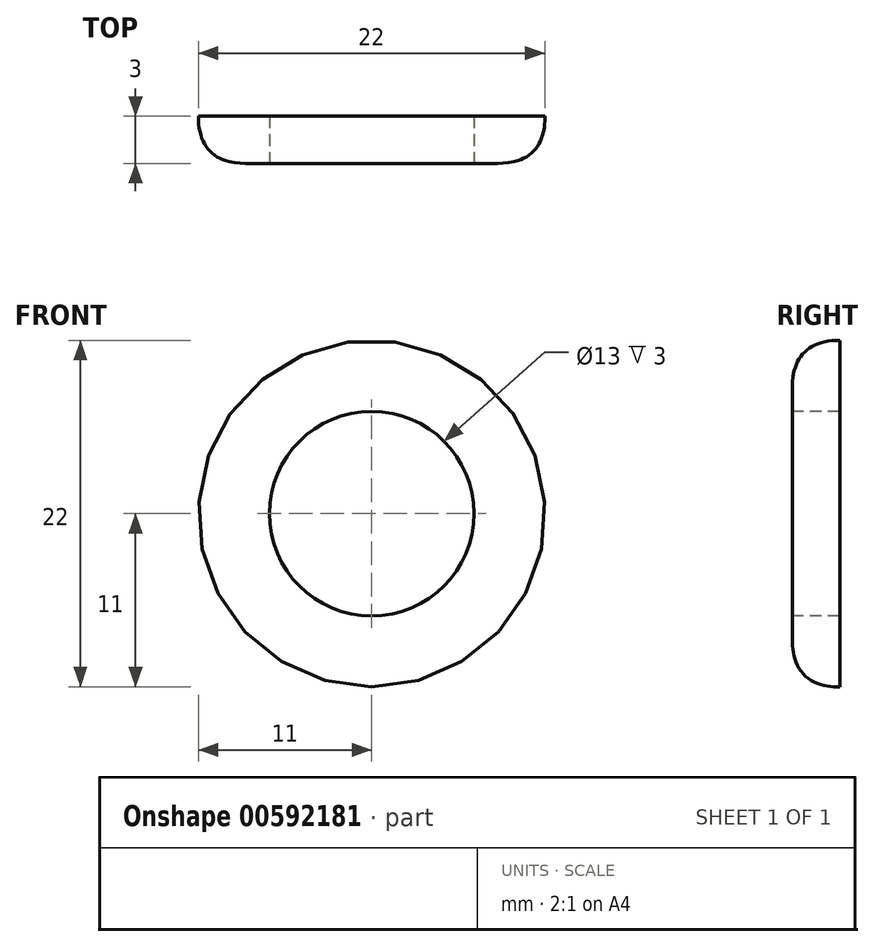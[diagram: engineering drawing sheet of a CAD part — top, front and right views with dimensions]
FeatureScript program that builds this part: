
annotation { "Feature Type Name" : "Feature", "Feature Type Description" : "" }
export const myFeature = defineFeature(function(context is Context, id is Id, definition is map)
    precondition{}
    {
        {
            var Q0;
            Q0=qCreatedBy(makeId("Front.planeOp"),FACE);
            var sketch = newSketch(context, id + "F0", { "sketchPlane" : qUnion([Q0])});
            skCircle(sketch, "E0", {"center": v(0, 0) * mm, "radius": 11 * mm});
            skSolve(sketch);
        }
        {
            var Q0;
            Q0 = qSketchRegion(id + "F0", true);
            extrude(context, id + "F1", {"entities" : qUnion([Q0]), "depth" : 3 * mm, "offsetDistance" : 25 * mm});
        }
        {
            var Q0;
            Q0=makeQuery(id+"F1.opExtrude","CAP_EDGE",EDGE,{"disambiguationData":[OSD([sQuery(id+"F0.wireOp",EDGE,"E0")])],"isStart":false});
            fillet(context, id + "F2", {"entities" : qUnion([Q0]), "tangentPropagation" : true, "crossSection" : FilletCrossSection.CURVATURE, "radius" : 3 * mm, "magnitude" : 0.5, "defaultsChanged" : false, "vertexSettings" : []});
        }
        {
            var Q0;
            Q0=makeQuery(id+"F1.opExtrude","CAP_FACE",FACE,{"disambiguationData":[OSD([sQuery(id+"F0.wireOp",EDGE,"E0")])],"isStart":false});
            var sketch = newSketch(context, id + "F3", { "sketchPlane" : qUnion([Q0])});
            skCircle(sketch, "E1", {"center": v(0, 0) * mm, "radius": 8 * mm});
            skSolve(sketch);
        }
        {
            var Q0;
            Q0=sQuery(id+"F3.wireOp",VERTEX,"E1.center");
            var Q1;
            Q1=makeQuery(id+"F1.opExtrude","SWEPT_BODY",BODY,{"disambiguationData":[OSD([sQuery(id+"F0.wireOp",EDGE,"E0")])]});
            hole(context, id + "F4", {"style" : HoleStyle.SIMPLE, "endStyle" : HoleEndStyle.BLIND, "holeDiameter" : 13 * mm, "majorDiameter" : 5 * mm, "holeDepth" : 12 * mm, "isTappedThrough" : true, "tappedDepth" : 12 * mm, "tapClearance" : 3, "startFromSketch" : true, "locations" : qUnion([Q0]), "scope" : qUnion([Q1])});
        }
    });
